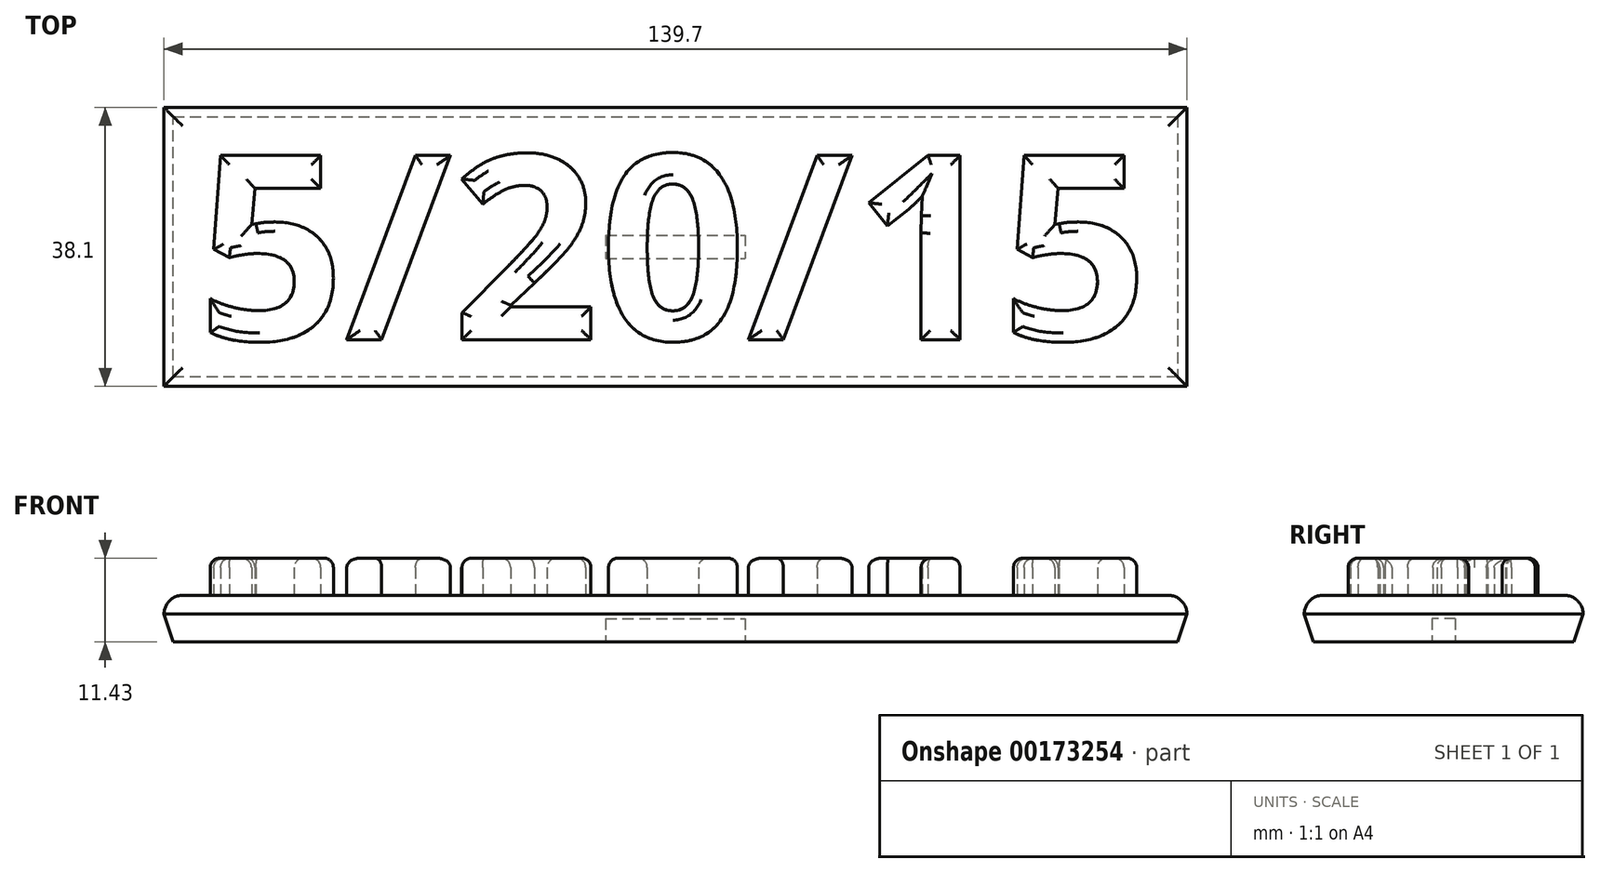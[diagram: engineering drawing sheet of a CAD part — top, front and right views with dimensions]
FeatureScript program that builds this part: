
annotation { "Feature Type Name" : "Feature", "Feature Type Description" : "" }
export const myFeature = defineFeature(function(context is Context, id is Id, definition is map)
    precondition{}
    {
        {
            var Q0;
            Q0=qCreatedBy(makeId("Top.planeOp"),FACE);
            var sketch = newSketch(context, id + "F0", { "sketchPlane" : qUnion([Q0])});
            skText(sketch, "E0", { "text": "5/20/15", "fontName": "OpenSans-Bold.ttf"});
            skLineSegment(sketch, "E1.bottom", {"start": v(69.85, 19.05) * mm, "end": v(-69.85, 19.05) * mm});
            skLineSegment(sketch, "E1.top", {"start": v(69.85, -19.05) * mm, "end": v(-69.85, -19.05) * mm});
            skLineSegment(sketch, "E1.left", {"start": v(69.85, 19.05) * mm, "end": v(69.85, -19.05) * mm});
            skLineSegment(sketch, "E1.right", {"start": v(-69.85, 19.05) * mm, "end": v(-69.85, -19.05) * mm});
            skPoint(sketch, "E1.middle", {"position": v(0, 0) * mm});
            const initialGuessF0  = {"E0": [-0.06527, -0.0127, 1, 0, 0.0254]};
            skSetInitialGuess(sketch, initialGuessF0);
            skSolve(sketch);
        }
        {
            var Q0;
            Q0=makeQuery(id+"F0.imprint","IMPRINT",FACE,{"disambiguationData":[TD([[makeQuery(id+"F0.imprint","IMPRINT",EDGE,{"derivedFrom":sQuery(id+"F0.wireOp",EDGE,"E0.sketch_text.stroke-0")}),-1.0]])]});
            var Q1;
            Q1=makeQuery(id+"F0.imprint","IMPRINT",FACE,{"disambiguationData":[TD([[makeQuery(id+"F0.imprint","IMPRINT",EDGE,{"derivedFrom":sQuery(id+"F0.wireOp",EDGE,"E0.sketch_text.stroke-24")}),-1.0]])]});
            var Q2;
            Q2=makeQuery(id+"F0.imprint","IMPRINT",FACE,{"disambiguationData":[TD([[makeQuery(id+"F0.imprint","IMPRINT",EDGE,{"derivedFrom":sQuery(id+"F0.wireOp",EDGE,"E0.sketch_text.stroke-48")}),-1.0]])]});
            var Q3;
            Q3=makeQuery(id+"F0.imprint","IMPRINT",FACE,{"disambiguationData":[TD([[makeQuery(id+"F0.imprint","IMPRINT",EDGE,{"derivedFrom":sQuery(id+"F0.wireOp",EDGE,"E0.sketch_text.stroke-64")}),-1.0]])]});
            var Q4;
            Q4=makeQuery(id+"F0.imprint","IMPRINT",FACE,{"disambiguationData":[TD([[makeQuery(id+"F0.imprint","IMPRINT",EDGE,{"derivedFrom":sQuery(id+"F0.wireOp",EDGE,"E0.sketch_text.stroke-68")}),-1.0]])]});
            var Q5;
            Q5=makeQuery(id+"F0.imprint","IMPRINT",FACE,{"disambiguationData":[TD([[makeQuery(id+"F0.imprint","IMPRINT",EDGE,{"derivedFrom":sQuery(id+"F0.wireOp",EDGE,"E0.sketch_text.stroke-78")}),-1.0]])]});
            var Q6;
            Q6=makeQuery(id+"F0.imprint","IMPRINT",FACE,{"disambiguationData":[TD([[makeQuery(id+"F0.imprint","IMPRINT",EDGE,{"derivedFrom":sQuery(id+"F0.wireOp",EDGE,"E0.sketch_text.stroke-20")}),-1.0]])]});
            extrude(context, id + "F1", {"entities" : qUnion([Q0, Q1, Q2, Q3, Q4, Q5, Q6]), "depth" : 5.08 * mm});
        }
        {
            var Q0;
            Q0=makeQuery(id+"F0.imprint","IMPRINT",FACE,{"disambiguationData":[TD([[makeQuery(id+"F0.imprint","IMPRINT",EDGE,{"derivedFrom":sQuery(id+"F0.wireOp",EDGE,"E0.sketch_text.stroke-0")}),1.0]])]});
            var Q1;
            Q1=makeQuery(id+"F0.imprint","IMPRINT",FACE,{"disambiguationData":[TD([[makeQuery(id+"F0.imprint","IMPRINT",EDGE,{"derivedFrom":sQuery(id+"F0.wireOp",EDGE,"E0.sketch_text.stroke-78")}),-1.0]])]});
            var Q2;
            Q2=makeQuery(id+"F0.imprint","IMPRINT",FACE,{"disambiguationData":[TD([[makeQuery(id+"F0.imprint","IMPRINT",EDGE,{"derivedFrom":sQuery(id+"F0.wireOp",EDGE,"E0.sketch_text.stroke-64")}),-1.0]])]});
            var Q3;
            Q3=makeQuery(id+"F0.imprint","IMPRINT",FACE,{"disambiguationData":[TD([[makeQuery(id+"F0.imprint","IMPRINT",EDGE,{"derivedFrom":sQuery(id+"F0.wireOp",EDGE,"E0.sketch_text.stroke-48")}),-1.0]])]});
            var Q4;
            Q4=makeQuery(id+"F0.imprint","IMPRINT",FACE,{"disambiguationData":[TD([[makeQuery(id+"F0.imprint","IMPRINT",EDGE,{"derivedFrom":sQuery(id+"F0.wireOp",EDGE,"E0.sketch_text.stroke-24")}),-1.0]])]});
            var Q5;
            Q5=makeQuery(id+"F0.imprint","IMPRINT",FACE,{"disambiguationData":[TD([[makeQuery(id+"F0.imprint","IMPRINT",EDGE,{"derivedFrom":sQuery(id+"F0.wireOp",EDGE,"E0.sketch_text.stroke-0")}),-1.0]])]});
            var Q6;
            Q6=makeQuery(id+"F0.imprint","IMPRINT",FACE,{"disambiguationData":[TD([[makeQuery(id+"F0.imprint","IMPRINT",EDGE,{"derivedFrom":sQuery(id+"F0.wireOp",EDGE,"E0.sketch_text.stroke-56")}),1.0]])]});
            var Q7;
            Q7=makeQuery(id+"F0.imprint","IMPRINT",FACE,{"disambiguationData":[TD([[makeQuery(id+"F0.imprint","IMPRINT",EDGE,{"derivedFrom":sQuery(id+"F0.wireOp",EDGE,"E0.sketch_text.stroke-95")}),1.0]])]});
            var Q8;
            Q8=makeQuery(id+"F0.imprint","IMPRINT",FACE,{"disambiguationData":[TD([[makeQuery(id+"F0.imprint","IMPRINT",EDGE,{"derivedFrom":sQuery(id+"F0.wireOp",EDGE,"E0.sketch_text.stroke-68")}),-1.0]])]});
            var Q9;
            Q9=makeQuery(id+"F0.imprint","IMPRINT",FACE,{"disambiguationData":[TD([[makeQuery(id+"F0.imprint","IMPRINT",EDGE,{"derivedFrom":sQuery(id+"F0.wireOp",EDGE,"E0.sketch_text.stroke-20")}),-1.0]])]});
            extrude(context, id + "F2", {"entities" : qUnion([Q0, Q1, Q2, Q3, Q4, Q5, Q6, Q7, Q8, Q9]), "oppositeDirection" : true, "depth" : 6.35 * mm});
        }
        {
            var Q0;
            Q0=makeQuery(id+"F1.opExtrude","CAP_FACE",FACE,{"disambiguationData":[OSD([sQuery(id+"F0.wireOp",EDGE,"E0.sketch_text.stroke-0"),sQuery(id+"F0.wireOp",EDGE,"E0.sketch_text.stroke-1"),sQuery(id+"F0.wireOp",EDGE,"E0.sketch_text.stroke-2"),sQuery(id+"F0.wireOp",EDGE,"E0.sketch_text.stroke-3"),sQuery(id+"F0.wireOp",EDGE,"E0.sketch_text.stroke-4"),sQuery(id+"F0.wireOp",EDGE,"E0.sketch_text.stroke-5"),sQuery(id+"F0.wireOp",EDGE,"E0.sketch_text.stroke-6"),sQuery(id+"F0.wireOp",EDGE,"E0.sketch_text.stroke-7"),sQuery(id+"F0.wireOp",EDGE,"E0.sketch_text.stroke-8"),sQuery(id+"F0.wireOp",EDGE,"E0.sketch_text.stroke-9"),sQuery(id+"F0.wireOp",EDGE,"E0.sketch_text.stroke-10"),sQuery(id+"F0.wireOp",EDGE,"E0.sketch_text.stroke-11"),sQuery(id+"F0.wireOp",EDGE,"E0.sketch_text.stroke-12"),sQuery(id+"F0.wireOp",EDGE,"E0.sketch_text.stroke-13"),sQuery(id+"F0.wireOp",EDGE,"E0.sketch_text.stroke-14"),sQuery(id+"F0.wireOp",EDGE,"E0.sketch_text.stroke-15"),sQuery(id+"F0.wireOp",EDGE,"E0.sketch_text.stroke-16"),sQuery(id+"F0.wireOp",EDGE,"E0.sketch_text.stroke-17"),sQuery(id+"F0.wireOp",EDGE,"E0.sketch_text.stroke-18"),sQuery(id+"F0.wireOp",EDGE,"E0.sketch_text.stroke-19")])],"isStart":false});
            var Q1;
            Q1=makeQuery(id+"F1.opExtrude","CAP_FACE",FACE,{"disambiguationData":[OSD([sQuery(id+"F0.wireOp",EDGE,"E0.sketch_text.stroke-20"),sQuery(id+"F0.wireOp",EDGE,"E0.sketch_text.stroke-21"),sQuery(id+"F0.wireOp",EDGE,"E0.sketch_text.stroke-22"),sQuery(id+"F0.wireOp",EDGE,"E0.sketch_text.stroke-23")])],"isStart":false});
            var Q2;
            Q2=makeQuery(id+"F1.opExtrude","CAP_FACE",FACE,{"disambiguationData":[OSD([sQuery(id+"F0.wireOp",EDGE,"E0.sketch_text.stroke-24"),sQuery(id+"F0.wireOp",EDGE,"E0.sketch_text.stroke-25"),sQuery(id+"F0.wireOp",EDGE,"E0.sketch_text.stroke-26"),sQuery(id+"F0.wireOp",EDGE,"E0.sketch_text.stroke-27"),sQuery(id+"F0.wireOp",EDGE,"E0.sketch_text.stroke-28"),sQuery(id+"F0.wireOp",EDGE,"E0.sketch_text.stroke-29"),sQuery(id+"F0.wireOp",EDGE,"E0.sketch_text.stroke-30"),sQuery(id+"F0.wireOp",EDGE,"E0.sketch_text.stroke-31"),sQuery(id+"F0.wireOp",EDGE,"E0.sketch_text.stroke-32"),sQuery(id+"F0.wireOp",EDGE,"E0.sketch_text.stroke-33"),sQuery(id+"F0.wireOp",EDGE,"E0.sketch_text.stroke-34"),sQuery(id+"F0.wireOp",EDGE,"E0.sketch_text.stroke-35"),sQuery(id+"F0.wireOp",EDGE,"E0.sketch_text.stroke-36"),sQuery(id+"F0.wireOp",EDGE,"E0.sketch_text.stroke-37"),sQuery(id+"F0.wireOp",EDGE,"E0.sketch_text.stroke-38"),sQuery(id+"F0.wireOp",EDGE,"E0.sketch_text.stroke-39"),sQuery(id+"F0.wireOp",EDGE,"E0.sketch_text.stroke-40"),sQuery(id+"F0.wireOp",EDGE,"E0.sketch_text.stroke-41"),sQuery(id+"F0.wireOp",EDGE,"E0.sketch_text.stroke-42"),sQuery(id+"F0.wireOp",EDGE,"E0.sketch_text.stroke-43"),sQuery(id+"F0.wireOp",EDGE,"E0.sketch_text.stroke-44"),sQuery(id+"F0.wireOp",EDGE,"E0.sketch_text.stroke-45"),sQuery(id+"F0.wireOp",EDGE,"E0.sketch_text.stroke-46"),sQuery(id+"F0.wireOp",EDGE,"E0.sketch_text.stroke-47")])],"isStart":false});
            var Q3;
            Q3=makeQuery(id+"F1.opExtrude","CAP_FACE",FACE,{"disambiguationData":[OSD([sQuery(id+"F0.wireOp",EDGE,"E0.sketch_text.stroke-48"),sQuery(id+"F0.wireOp",EDGE,"E0.sketch_text.stroke-49"),sQuery(id+"F0.wireOp",EDGE,"E0.sketch_text.stroke-50"),sQuery(id+"F0.wireOp",EDGE,"E0.sketch_text.stroke-51"),sQuery(id+"F0.wireOp",EDGE,"E0.sketch_text.stroke-52"),sQuery(id+"F0.wireOp",EDGE,"E0.sketch_text.stroke-53"),sQuery(id+"F0.wireOp",EDGE,"E0.sketch_text.stroke-54"),sQuery(id+"F0.wireOp",EDGE,"E0.sketch_text.stroke-55"),sQuery(id+"F0.wireOp",EDGE,"E0.sketch_text.stroke-56"),sQuery(id+"F0.wireOp",EDGE,"E0.sketch_text.stroke-57"),sQuery(id+"F0.wireOp",EDGE,"E0.sketch_text.stroke-58"),sQuery(id+"F0.wireOp",EDGE,"E0.sketch_text.stroke-59"),sQuery(id+"F0.wireOp",EDGE,"E0.sketch_text.stroke-60"),sQuery(id+"F0.wireOp",EDGE,"E0.sketch_text.stroke-61"),sQuery(id+"F0.wireOp",EDGE,"E0.sketch_text.stroke-62"),sQuery(id+"F0.wireOp",EDGE,"E0.sketch_text.stroke-63")])],"isStart":false});
            var Q4;
            Q4=makeQuery(id+"F1.opExtrude","CAP_FACE",FACE,{"disambiguationData":[OSD([sQuery(id+"F0.wireOp",EDGE,"E0.sketch_text.stroke-64"),sQuery(id+"F0.wireOp",EDGE,"E0.sketch_text.stroke-65"),sQuery(id+"F0.wireOp",EDGE,"E0.sketch_text.stroke-66"),sQuery(id+"F0.wireOp",EDGE,"E0.sketch_text.stroke-67")])],"isStart":false});
            var Q5;
            Q5=makeQuery(id+"F1.opExtrude","CAP_FACE",FACE,{"disambiguationData":[OSD([sQuery(id+"F0.wireOp",EDGE,"E0.sketch_text.stroke-68"),sQuery(id+"F0.wireOp",EDGE,"E0.sketch_text.stroke-69"),sQuery(id+"F0.wireOp",EDGE,"E0.sketch_text.stroke-70"),sQuery(id+"F0.wireOp",EDGE,"E0.sketch_text.stroke-71"),sQuery(id+"F0.wireOp",EDGE,"E0.sketch_text.stroke-72"),sQuery(id+"F0.wireOp",EDGE,"E0.sketch_text.stroke-73"),sQuery(id+"F0.wireOp",EDGE,"E0.sketch_text.stroke-74"),sQuery(id+"F0.wireOp",EDGE,"E0.sketch_text.stroke-75"),sQuery(id+"F0.wireOp",EDGE,"E0.sketch_text.stroke-76"),sQuery(id+"F0.wireOp",EDGE,"E0.sketch_text.stroke-77")])],"isStart":false});
            var Q6;
            Q6=makeQuery(id+"F1.opExtrude","CAP_FACE",FACE,{"disambiguationData":[OSD([sQuery(id+"F0.wireOp",EDGE,"E0.sketch_text.stroke-78"),sQuery(id+"F0.wireOp",EDGE,"E0.sketch_text.stroke-79"),sQuery(id+"F0.wireOp",EDGE,"E0.sketch_text.stroke-80"),sQuery(id+"F0.wireOp",EDGE,"E0.sketch_text.stroke-81"),sQuery(id+"F0.wireOp",EDGE,"E0.sketch_text.stroke-82"),sQuery(id+"F0.wireOp",EDGE,"E0.sketch_text.stroke-83"),sQuery(id+"F0.wireOp",EDGE,"E0.sketch_text.stroke-84"),sQuery(id+"F0.wireOp",EDGE,"E0.sketch_text.stroke-85"),sQuery(id+"F0.wireOp",EDGE,"E0.sketch_text.stroke-86"),sQuery(id+"F0.wireOp",EDGE,"E0.sketch_text.stroke-87"),sQuery(id+"F0.wireOp",EDGE,"E0.sketch_text.stroke-88"),sQuery(id+"F0.wireOp",EDGE,"E0.sketch_text.stroke-89"),sQuery(id+"F0.wireOp",EDGE,"E0.sketch_text.stroke-90"),sQuery(id+"F0.wireOp",EDGE,"E0.sketch_text.stroke-91"),sQuery(id+"F0.wireOp",EDGE,"E0.sketch_text.stroke-92"),sQuery(id+"F0.wireOp",EDGE,"E0.sketch_text.stroke-93"),sQuery(id+"F0.wireOp",EDGE,"E0.sketch_text.stroke-94"),sQuery(id+"F0.wireOp",EDGE,"E0.sketch_text.stroke-95"),sQuery(id+"F0.wireOp",EDGE,"E0.sketch_text.stroke-96"),sQuery(id+"F0.wireOp",EDGE,"E0.sketch_text.stroke-97")])],"isStart":false});
            fillet(context, id + "F3", {"entities" : qUnion([Q0, Q1, Q2, Q3, Q4, Q5, Q6]), "radius" : 1.27 * mm, "tangentPropagation" : true, "allowEdgeOverflow" : false});
        }
        {
            var Q0;
            Q0=makeQuery(id+"F2.opExtrude","CAP_FACE",FACE,{"disambiguationData":[OSD([sQuery(id+"F0.wireOp",EDGE,"E1.bottom"),sQuery(id+"F0.wireOp",EDGE,"E1.top"),sQuery(id+"F0.wireOp",EDGE,"E1.left"),sQuery(id+"F0.wireOp",EDGE,"E1.right")])],"isStart":false});
            var sketch = newSketch(context, id + "F4", { "sketchPlane" : qUnion([Q0])});
            skLineSegment(sketch, "E2.bottom", {"start": v(-9.53, -1.59) * mm, "end": v(9.53, -1.59) * mm});
            skLineSegment(sketch, "E2.top", {"start": v(-9.53, 1.59) * mm, "end": v(9.53, 1.59) * mm});
            skLineSegment(sketch, "E2.left", {"start": v(-9.53, -1.59) * mm, "end": v(-9.53, 1.59) * mm});
            skLineSegment(sketch, "E2.right", {"start": v(9.53, -1.59) * mm, "end": v(9.53, 1.59) * mm});
            skPoint(sketch, "E2.middle", {"position": v(0, 0) * mm});
            skSolve(sketch);
        }
        {
            var Q0;
            Q0 = qSketchRegion(id + "F4", true);
            extrude(context, id + "F5", {"entities" : qUnion([Q0]), "operationType" : NewBodyOperationType.REMOVE, "oppositeDirection" : true, "depth" : 3.17 * mm});
        }
        {
            var Q0;
            Q0=makeQuery(id+"F2.opExtrude","CAP_EDGE",EDGE,{"disambiguationData":[OSD([sQuery(id+"F0.wireOp",EDGE,"E1.left")])],"isStart":true});
            var Q1;
            Q1=makeQuery(id+"F2.opExtrude","CAP_EDGE",EDGE,{"disambiguationData":[OSD([sQuery(id+"F0.wireOp",EDGE,"E1.bottom")])],"isStart":true});
            var Q2;
            Q2=makeQuery(id+"F2.opExtrude","CAP_EDGE",EDGE,{"disambiguationData":[OSD([sQuery(id+"F0.wireOp",EDGE,"E1.right")])],"isStart":true});
            var Q3;
            Q3=makeQuery(id+"F2.opExtrude","CAP_EDGE",EDGE,{"disambiguationData":[OSD([sQuery(id+"F0.wireOp",EDGE,"E1.top")])],"isStart":true});
            fillet(context, id + "F6", {"entities" : qUnion([Q0, Q1, Q2, Q3]), "radius" : 2.54 * mm, "tangentPropagation" : true, "allowEdgeOverflow" : false});
        }
        {
            var Q0;
            Q0=makeQuery(id+"F2.opExtrude","CAP_EDGE",EDGE,{"disambiguationData":[OSD([sQuery(id+"F0.wireOp",EDGE,"E1.top")])],"isStart":false});
            var Q1;
            Q1=makeQuery(id+"F2.opExtrude","CAP_EDGE",EDGE,{"disambiguationData":[OSD([sQuery(id+"F0.wireOp",EDGE,"E1.left")])],"isStart":false});
            var Q2;
            Q2=makeQuery(id+"F2.opExtrude","CAP_EDGE",EDGE,{"disambiguationData":[OSD([sQuery(id+"F0.wireOp",EDGE,"E1.bottom")])],"isStart":false});
            var Q3;
            Q3=makeQuery(id+"F2.opExtrude","CAP_EDGE",EDGE,{"disambiguationData":[OSD([sQuery(id+"F0.wireOp",EDGE,"E1.right")])],"isStart":false});
            chamfer(context, id + "F7", {"entities" : qUnion([Q0, Q1, Q2, Q3]), "chamferType" : ChamferType.TWO_OFFSETS, "width1" : 1.27 * mm, "oppositeDirection" : false, "width2" : 3.8 * mm, "tangentPropagation" : true});
        }
    });
